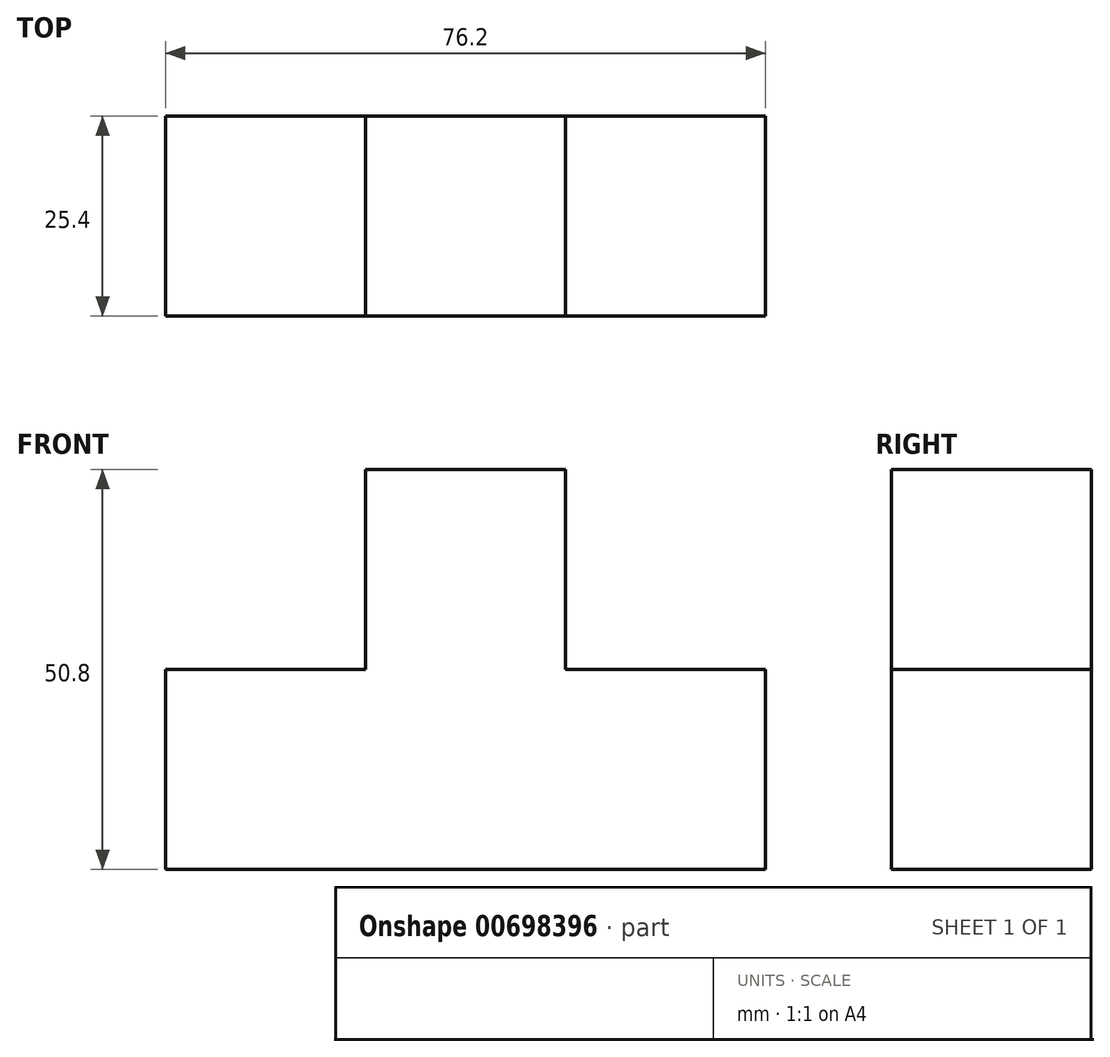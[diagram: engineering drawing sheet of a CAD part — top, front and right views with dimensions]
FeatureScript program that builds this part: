
annotation { "Feature Type Name" : "Feature", "Feature Type Description" : "" }
export const myFeature = defineFeature(function(context is Context, id is Id, definition is map)
    precondition{}
    {
        {
            var Q0;
            Q0=qCreatedBy(makeId("Front.planeOp"),FACE);
            var sketch = newSketch(context, id + "F0", { "sketchPlane" : qUnion([Q0])});
            skLineSegment(sketch, "E0.bottom", {"start": v(0, 25.4) * mm, "end": v(25.4, 25.4) * mm});
            skLineSegment(sketch, "E0.top", {"start": v(0, 0) * mm, "end": v(25.4, 0) * mm});
            skLineSegment(sketch, "E0.left", {"start": v(0, 25.4) * mm, "end": v(0, 0) * mm});
            skLineSegment(sketch, "E0.right", {"start": v(25.4, 25.4) * mm, "end": v(25.4, 0) * mm});
            skLineSegment(sketch, "E1.bottom", {"start": v(0, 25.4) * mm, "end": v(-25.4, 25.4) * mm});
            skLineSegment(sketch, "E1.top", {"start": v(0, 0) * mm, "end": v(-25.4, 0) * mm});
            skLineSegment(sketch, "E1.right", {"start": v(-25.4, 25.4) * mm, "end": v(-25.4, 0) * mm});
            skLineSegment(sketch, "E2.bottom", {"start": v(-25.4, 25.4) * mm, "end": v(-50.8, 25.4) * mm});
            skLineSegment(sketch, "E2.top", {"start": v(-25.4, 0) * mm, "end": v(-50.8, 0) * mm});
            skLineSegment(sketch, "E2.right", {"start": v(-50.8, 25.4) * mm, "end": v(-50.8, 0) * mm});
            skLineSegment(sketch, "E3.top", {"start": v(0, 50.8) * mm, "end": v(-25.4, 50.8) * mm});
            skLineSegment(sketch, "E3.left", {"start": v(0, 25.4) * mm, "end": v(0, 50.8) * mm});
            skLineSegment(sketch, "E3.right", {"start": v(-25.4, 25.4) * mm, "end": v(-25.4, 50.8) * mm});
            skSolve(sketch);
        }
        {
            var Q0;
            Q0 = qSketchRegion(id + "F0", true);
            extrude(context, id + "F1", {"entities" : qUnion([Q0]), "depth" : 25.4 * mm, "offsetDistance" : 25.4 * mm});
        }
    });
